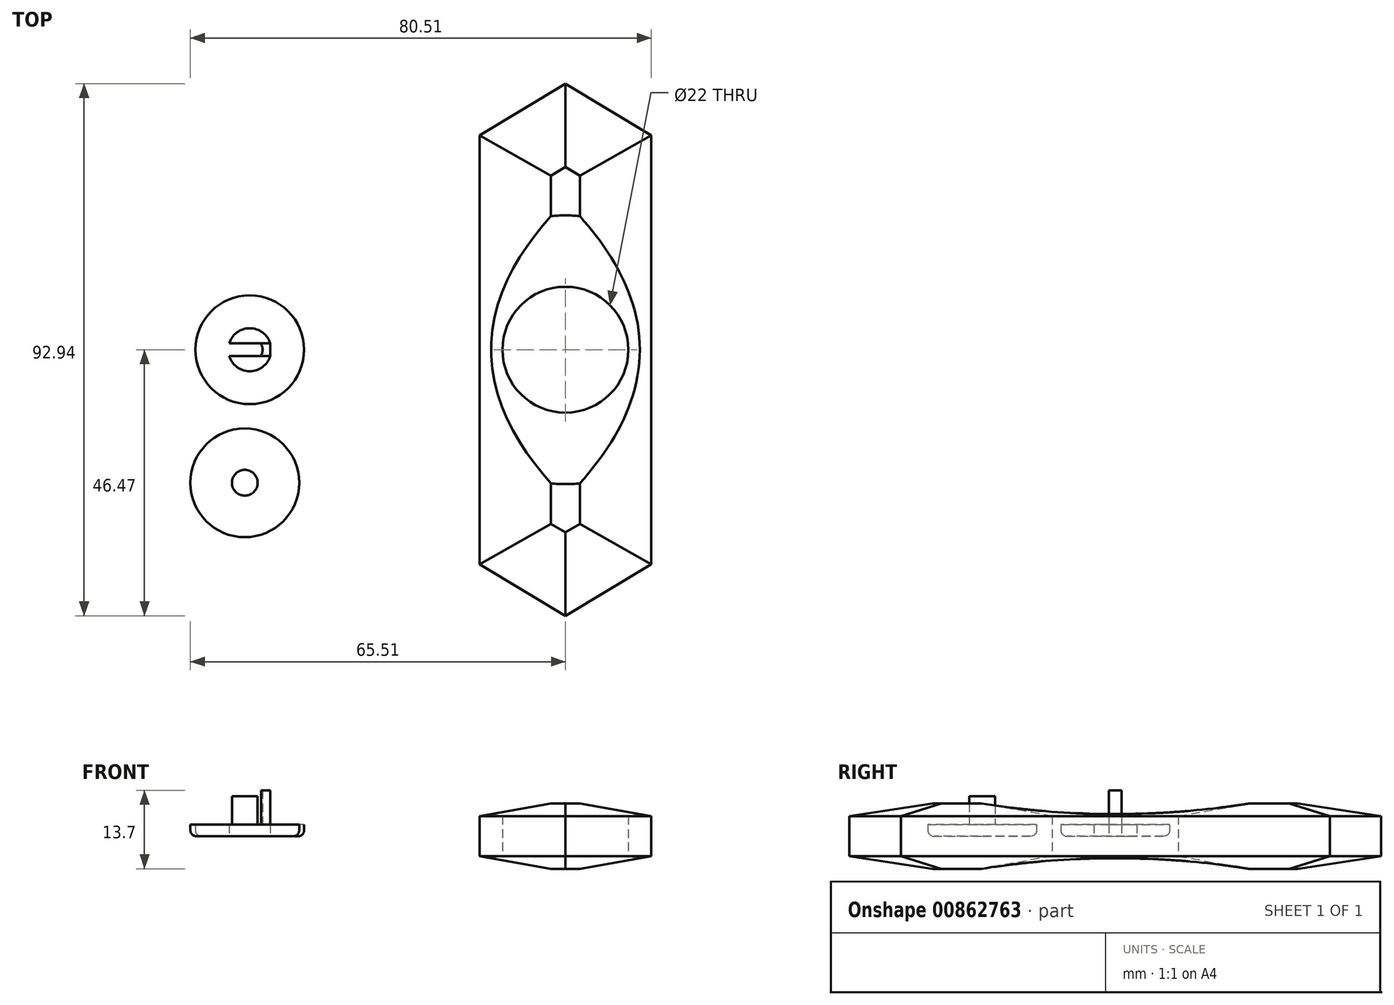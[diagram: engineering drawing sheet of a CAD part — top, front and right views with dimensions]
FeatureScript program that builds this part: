
annotation { "Feature Type Name" : "Feature", "Feature Type Description" : "" }
export const myFeature = defineFeature(function(context is Context, id is Id, definition is map)
    precondition{}
    {
        {
            var Q0;
            Q0=qCreatedBy(makeId("Top.planeOp"),FACE);
            var sketch = newSketch(context, id + "F0", { "sketchPlane" : qUnion([Q0])});
            skCircle(sketch, "E0", {"center": v(0, 0) * mm, "radius": 11 * mm});
            skLineSegment(sketch, "E1.left", {"start": v(15, -37.47) * mm, "end": v(15, 37.47) * mm});
            skLineSegment(sketch, "E1.right", {"start": v(-15, -37.47) * mm, "end": v(-15, 37.47) * mm});
            skLineSegment(sketch, "E2", {"start": v(-15, 37.47) * mm, "end": v(0, 46.47) * mm});
            skLineSegment(sketch, "E3", {"start": v(0, 46.47) * mm, "end": v(15, 37.47) * mm});
            skLineSegment(sketch, "E4", {"start": v(-15, -37.47) * mm, "end": v(0, -46.47) * mm});
            skLineSegment(sketch, "E5", {"start": v(0, -46.47) * mm, "end": v(15, -37.47) * mm});
            skSolve(sketch);
        }
        {
            var Q0;
            {var subQ0=sQuery(id+"F0.wireOp",EDGE,"E1.right");var subQ1=sQuery(id+"F0.wireOp",EDGE,"E1.top");var subQ2=makeQuery(id+"F0.imprint","INTERSECT",VERTEX,{"derivedFrom":[subQ1,subQ0]});Q0=makeQuery(id+"F0.imprint","IMPRINT",FACE,{"disambiguationData":[TD([[makeQuery(id+"F0.imprint","IMPRINT",EDGE,{"disambiguationData":[TD([[subQ2,1.0]])],"derivedFrom":subQ1}),1.0]])]});}
            var Q1;
            Q1=makeQuery(id+"F0.imprint","IMPRINT",FACE,{"disambiguationData":[TD([[makeQuery(id+"F0.imprint","IMPRINT",EDGE,{"derivedFrom":sQuery(id+"F0.wireOp",EDGE,"E0")}),-1.0]])]});
            var Q2;
            {var subQ0=sQuery(id+"F0.wireOp",EDGE,"XqkOnmEN-YKPt-X9L8-qTjw-NtbxfFgccqZy");var subQ1=sQuery(id+"F0.wireOp",EDGE,"E1.left");var subQ2=makeQuery(id+"F0.imprint","INTERSECT",VERTEX,{"disambiguationData":[OD(0.0)],"derivedFrom":[subQ1,subQ0]});Q2=makeQuery(id+"F0.imprint","IMPRINT",FACE,{"disambiguationData":[TD([[makeQuery(id+"F0.imprint","IMPRINT",EDGE,{"disambiguationData":[TD([[subQ2,-1.0]])],"derivedFrom":subQ1}),1.0]])]});}
            var Q3;
            {var subQ0=sQuery(id+"F0.wireOp",EDGE,"E1.left");var subQ1=sQuery(id+"F0.wireOp",EDGE,"E1.bottom");var subQ2=makeQuery(id+"F0.imprint","INTERSECT",VERTEX,{"derivedFrom":[subQ1,subQ0]});Q3=makeQuery(id+"F0.imprint","IMPRINT",FACE,{"disambiguationData":[TD([[makeQuery(id+"F0.imprint","IMPRINT",EDGE,{"disambiguationData":[TD([[subQ2,-1.0]])],"derivedFrom":subQ1}),-1.0]])]});}
            var Q4;
            {var subQ0=sQuery(id+"F0.wireOp",EDGE,"xUuo6eMj-NljG-XD0U-LhTG-hYgstR9SnbR7");var subQ1=sQuery(id+"F0.wireOp",EDGE,"E1.right");var subQ2=makeQuery(id+"F0.imprint","INTERSECT",VERTEX,{"disambiguationData":[OD(0.0)],"derivedFrom":[subQ1,subQ0]});Q4=makeQuery(id+"F0.imprint","IMPRINT",FACE,{"disambiguationData":[TD([[makeQuery(id+"F0.imprint","IMPRINT",EDGE,{"disambiguationData":[TD([[subQ2,-1.0]])],"derivedFrom":subQ1}),-1.0]])]});}
            var Q5;
            {var subQ0=sQuery(id+"F0.wireOp",EDGE,"XqkOnmEN-YKPt-X9L8-qTjw-NtbxfFgccqZy");var subQ1=sQuery(id+"F0.wireOp",EDGE,"E1.right");var subQ2=makeQuery(id+"F0.imprint","INTERSECT",VERTEX,{"disambiguationData":[OD(1.0)],"derivedFrom":[subQ1,subQ0]});Q5=makeQuery(id+"F0.imprint","IMPRINT",FACE,{"disambiguationData":[TD([[makeQuery(id+"F0.imprint","IMPRINT",EDGE,{"disambiguationData":[TD([[subQ2,-1.0]])],"derivedFrom":subQ1}),-1.0]])]});}
            var Q6;
            {var subQ0=sQuery(id+"F0.wireOp",EDGE,"XqkOnmEN-YKPt-X9L8-qTjw-NtbxfFgccqZy");var subQ1=sQuery(id+"F0.wireOp",EDGE,"E1.top");var subQ2=makeQuery(id+"F0.imprint","INTERSECT",VERTEX,{"derivedFrom":[subQ1,subQ0]});Q6=makeQuery(id+"F0.imprint","IMPRINT",FACE,{"disambiguationData":[TD([[makeQuery(id+"F0.imprint","IMPRINT",EDGE,{"disambiguationData":[TD([[subQ2,-1.0]])],"derivedFrom":subQ1}),1.0]])]});}
            var Q7;
            {var subQ0=sQuery(id+"F0.wireOp",EDGE,"E1.left");var subQ1=sQuery(id+"F0.wireOp",EDGE,"E1.top");var subQ2=makeQuery(id+"F0.imprint","INTERSECT",VERTEX,{"derivedFrom":[subQ1,subQ0]});Q7=makeQuery(id+"F0.imprint","IMPRINT",FACE,{"disambiguationData":[TD([[makeQuery(id+"F0.imprint","IMPRINT",EDGE,{"disambiguationData":[TD([[subQ2,-1.0]])],"derivedFrom":subQ1}),1.0]])]});}
            var Q8;
            {var subQ0=sQuery(id+"F0.wireOp",EDGE,"OLPtJjKp-UBlK-7H81-Stp1-wvhKm3npHkhX");var subQ1=sQuery(id+"F0.wireOp",EDGE,"E1.left");var subQ2=makeQuery(id+"F0.imprint","INTERSECT",VERTEX,{"disambiguationData":[OD(0.0)],"derivedFrom":[subQ1,subQ0]});Q8=makeQuery(id+"F0.imprint","IMPRINT",FACE,{"disambiguationData":[TD([[makeQuery(id+"F0.imprint","IMPRINT",EDGE,{"disambiguationData":[TD([[subQ2,-1.0]])],"derivedFrom":subQ1}),1.0]])]});}
            var Q9;
            {var subQ0=sQuery(id+"F0.wireOp",EDGE,"E1.right");var subQ1=sQuery(id+"F0.wireOp",EDGE,"E1.bottom");var subQ2=makeQuery(id+"F0.imprint","INTERSECT",VERTEX,{"derivedFrom":[subQ1,subQ0]});Q9=makeQuery(id+"F0.imprint","IMPRINT",FACE,{"disambiguationData":[TD([[makeQuery(id+"F0.imprint","IMPRINT",EDGE,{"disambiguationData":[TD([[subQ2,1.0]])],"derivedFrom":subQ1}),-1.0]])]});}
            var Q10;
            {var subQ0=sQuery(id+"F0.wireOp",EDGE,"XqkOnmEN-YKPt-X9L8-qTjw-NtbxfFgccqZy");var subQ1=sQuery(id+"F0.wireOp",EDGE,"E1.bottom");var subQ2=makeQuery(id+"F0.imprint","INTERSECT",VERTEX,{"derivedFrom":[subQ1,subQ0]});Q10=makeQuery(id+"F0.imprint","IMPRINT",FACE,{"disambiguationData":[TD([[makeQuery(id+"F0.imprint","IMPRINT",EDGE,{"disambiguationData":[TD([[subQ2,-1.0]])],"derivedFrom":subQ1}),-1.0]])]});}
            var Q11;
            {var subQ0=sQuery(id+"F0.wireOp",EDGE,"tDE5TlyR-l5bq-vjll-LGqx-ABghjxnvdLlJ");var subQ1=sQuery(id+"F0.wireOp",EDGE,"E1.left");var subQ2=makeQuery(id+"F0.imprint","INTERSECT",VERTEX,{"disambiguationData":[OD(0.0)],"derivedFrom":[subQ1,subQ0]});Q11=makeQuery(id+"F0.imprint","IMPRINT",FACE,{"disambiguationData":[TD([[makeQuery(id+"F0.imprint","IMPRINT",EDGE,{"disambiguationData":[TD([[subQ2,-1.0]])],"derivedFrom":subQ1}),1.0]])]});}
            var Q12;
            {var subQ1=sQuery(id+"F0.wireOp",EDGE,"XqkOnmEN-YKPt-X9L8-qTjw-NtbxfFgccqZy");var subQ3=sQuery(id+"F0.wireOp",EDGE,"E1.bottom");var subQ4=makeQuery(id+"F0.imprint","INTERSECT",VERTEX,{"derivedFrom":[subQ3,subQ1]});Q12=makeQuery(id+"F0.imprint","IMPRINT",FACE,{"disambiguationData":[TD([[makeQuery(id+"F0.imprint","IMPRINT",EDGE,{"disambiguationData":[TD([[subQ4,-1.0]])],"derivedFrom":subQ3}),1.0]])]});}
            var Q13;
            {var subQ5=sQuery(id+"F0.wireOp",EDGE,"XqkOnmEN-YKPt-X9L8-qTjw-NtbxfFgccqZy");var subQ7=sQuery(id+"F0.wireOp",EDGE,"E1.top");var subQ8=makeQuery(id+"F0.imprint","INTERSECT",VERTEX,{"derivedFrom":[subQ7,subQ5]});Q13=makeQuery(id+"F0.imprint","IMPRINT",FACE,{"disambiguationData":[TD([[makeQuery(id+"F0.imprint","IMPRINT",EDGE,{"disambiguationData":[TD([[subQ8,-1.0]])],"derivedFrom":subQ7}),-1.0]])]});}
            extrude(context, id + "F1", {"entities" : qUnion([Q0, Q1, Q2, Q3, Q4, Q5, Q6, Q7, Q8, Q9, Q10, Q11, Q12, Q13]), "endBound" : BoundingType.SYMMETRIC, "depth" : 7 * mm, "offsetDistance" : 25 * mm});
        }
        {
            var Q0;
            Q0=qCreatedBy(makeId("Top.planeOp"),FACE);
            var sketch = newSketch(context, id + "F2", { "sketchPlane" : qUnion([Q0])});
            skCircle(sketch, "E6", {"center": v(-55.14, 0) * mm, "radius": 3.75 * mm});
            skCircle(sketch, "E7", {"center": v(-55.14, 0) * mm, "radius": 2.25 * mm});
            skCircle(sketch, "E8", {"center": v(-55.14, 0) * mm, "radius": 9.5 * mm});
            skLineSegment(sketch, "E9.bottom", {"start": v(-51.56, -1.1) * mm, "end": v(-58.73, -1.1) * mm});
            skLineSegment(sketch, "E9.top", {"start": v(-51.56, 1.1) * mm, "end": v(-58.73, 1.1) * mm});
            skLineSegment(sketch, "E9.left", {"start": v(-51.56, -1.1) * mm, "end": v(-51.56, 1.1) * mm});
            skLineSegment(sketch, "E9.right", {"start": v(-58.73, -1.1) * mm, "end": v(-58.73, 1.1) * mm});
            skSolve(sketch);
        }
        {
            var Q0;
            {var subQ0=sQuery(id+"F2.wireOp",EDGE,"E9.bottom");var subQ4=sQuery(id+"F2.wireOp",EDGE,"E7");var subQ5=makeQuery(id+"F2.imprint","INTERSECT",VERTEX,{"disambiguationData":[OD(0.0)],"derivedFrom":[subQ4,subQ0]});Q0=makeQuery(id+"F2.imprint","IMPRINT",FACE,{"disambiguationData":[TD([[makeQuery(id+"F2.imprint","IMPRINT",EDGE,{"disambiguationData":[TD([[subQ5,-1.0]])],"derivedFrom":subQ4}),-1.0]])]});}
            var Q1;
            {var subQ0=sQuery(id+"F2.wireOp",EDGE,"E9.top");var subQ4=sQuery(id+"F2.wireOp",EDGE,"E7");var subQ5=makeQuery(id+"F2.imprint","INTERSECT",VERTEX,{"disambiguationData":[OD(0.0)],"derivedFrom":[subQ4,subQ0]});Q1=makeQuery(id+"F2.imprint","IMPRINT",FACE,{"disambiguationData":[TD([[makeQuery(id+"F2.imprint","IMPRINT",EDGE,{"disambiguationData":[TD([[subQ5,1.0]])],"derivedFrom":subQ4}),-1.0]])]});}
            extrude(context, id + "F3", {"entities" : qUnion([Q0, Q1]), "depth" : 8 * mm, "offsetDistance" : 25 * mm});
        }
        {
            var Q0;
            Q0 = qSketchRegion(id + "F2", true);
            var Q1;
            Q1=makeQuery(id+"F2.imprint","IMPRINT",FACE,{"disambiguationData":[TD([[makeQuery(id+"F2.imprint","IMPRINT",EDGE,{"derivedFrom":sQuery(id+"F2.wireOp",EDGE,"E7")}),1.0]])]});
            var Q2;
            {var subQ5=sQuery(id+"F2.wireOp",EDGE,"E9.left");Q2=makeQuery(id+"F2.imprint","IMPRINT",FACE,{"disambiguationData":[TD([[makeQuery(id+"F2.imprint","IMPRINT",EDGE,{"derivedFrom":subQ5}),1.0]])]});}
            var Q3;
            {var subQ0=sQuery(id+"F2.wireOp",EDGE,"E9.top");var subQ1=sQuery(id+"F2.wireOp",EDGE,"E7");var subQ2=makeQuery(id+"F2.imprint","INTERSECT",VERTEX,{"disambiguationData":[OD(0.0)],"derivedFrom":[subQ1,subQ0]});Q3=makeQuery(id+"F2.imprint","IMPRINT",FACE,{"disambiguationData":[TD([[makeQuery(id+"F2.imprint","IMPRINT",EDGE,{"disambiguationData":[TD([[subQ2,1.0]])],"derivedFrom":subQ1}),1.0]])]});}
            var Q4;
            {var subQ0=sQuery(id+"F2.wireOp",EDGE,"E9.bottom");var subQ1=sQuery(id+"F2.wireOp",EDGE,"E7");var subQ2=makeQuery(id+"F2.imprint","INTERSECT",VERTEX,{"disambiguationData":[OD(0.0)],"derivedFrom":[subQ1,subQ0]});Q4=makeQuery(id+"F2.imprint","IMPRINT",FACE,{"disambiguationData":[TD([[makeQuery(id+"F2.imprint","IMPRINT",EDGE,{"disambiguationData":[TD([[subQ2,-1.0]])],"derivedFrom":subQ1}),1.0]])]});}
            var Q5;
            {var subQ0=sQuery(id+"F2.wireOp",EDGE,"E9.right");Q5=makeQuery(id+"F2.imprint","IMPRINT",FACE,{"disambiguationData":[TD([[makeQuery(id+"F2.imprint","IMPRINT",EDGE,{"derivedFrom":subQ0}),1.0]])]});}
            var Q6;
            {var subQ5=sQuery(id+"F2.wireOp",EDGE,"E9.right");Q6=makeQuery(id+"F2.imprint","IMPRINT",FACE,{"disambiguationData":[TD([[makeQuery(id+"F2.imprint","IMPRINT",EDGE,{"derivedFrom":subQ5}),-1.0]])]});}
            var Q7;
            {var subQ0=sQuery(id+"F2.wireOp",EDGE,"E9.left");Q7=makeQuery(id+"F2.imprint","IMPRINT",FACE,{"disambiguationData":[TD([[makeQuery(id+"F2.imprint","IMPRINT",EDGE,{"derivedFrom":subQ0}),-1.0]])]});}
            extrude(context, id + "F4", {"entities" : qUnion([Q0, Q1, Q2, Q3, Q4, Q5, Q6, Q7]), "operationType" : NewBodyOperationType.ADD, "depth" : 2 * mm, "offsetDistance" : 25 * mm});
        }
        {
            var Q0;
            Q0=makeQuery(id+"F4.opExtrude","CAP_EDGE",EDGE,{"disambiguationData":[OSD([sQuery(id+"F2.wireOp",EDGE,"E8")])],"isStart":true});
            fillet(context, id + "F5", {"entities" : qUnion([Q0]), "radius" : 1 * mm, "tangentPropagation" : true, "allowEdgeOverflow" : false});
        }
        {
            var Q0;
            Q0=qCreatedBy(makeId("Top.planeOp"),FACE);
            var sketch = newSketch(context, id + "F6", { "sketchPlane" : qUnion([Q0])});
            skCircle(sketch, "E10", {"center": v(-56, -23.24) * mm, "radius": 2.25 * mm});
            skCircle(sketch, "E11", {"center": v(-56, -23.24) * mm, "radius": 9.5 * mm});
            skSolve(sketch);
        }
        {
            var Q0;
            Q0=makeQuery(id+"F6.imprint","IMPRINT",FACE,{"disambiguationData":[TD([[makeQuery(id+"F6.imprint","IMPRINT",EDGE,{"derivedFrom":sQuery(id+"F6.wireOp",EDGE,"E10")}),-1.0]])]});
            extrude(context, id + "F7", {"entities" : qUnion([Q0]), "depth" : 2 * mm, "offsetDistance" : 25 * mm});
        }
        {
            var Q0;
            Q0=makeQuery(id+"F6.imprint","IMPRINT",FACE,{"disambiguationData":[TD([[makeQuery(id+"F6.imprint","IMPRINT",EDGE,{"derivedFrom":sQuery(id+"F6.wireOp",EDGE,"E10")}),1.0]])]});
            extrude(context, id + "F8", {"entities" : qUnion([Q0]), "operationType" : NewBodyOperationType.ADD, "depth" : 7 * mm, "offsetDistance" : 25 * mm});
        }
        {
            var Q0;
            Q0=makeQuery(id+"F7.opExtrude","CAP_EDGE",EDGE,{"disambiguationData":[OSD([sQuery(id+"F6.wireOp",EDGE,"E11")])],"isStart":true});
            fillet(context, id + "F9", {"entities" : qUnion([Q0]), "radius" : 1 * mm, "tangentPropagation" : true, "allowEdgeOverflow" : false});
        }
        {
            var Q0;
            Q0=makeQuery(id+"F1.opExtrude","CAP_FACE",FACE,{"disambiguationData":[OSD([sQuery(id+"F0.wireOp",EDGE,"E0"),sQuery(id+"F0.wireOp",EDGE,"E1.left"),sQuery(id+"F0.wireOp",EDGE,"E1.right"),sQuery(id+"F0.wireOp",EDGE,"E2"),sQuery(id+"F0.wireOp",EDGE,"E3"),sQuery(id+"F0.wireOp",EDGE,"E4"),sQuery(id+"F0.wireOp",EDGE,"E5")])],"isStart":false});
            var Q1;
            Q1=makeQuery(id+"F1.opExtrude","CAP_FACE",FACE,{"disambiguationData":[OSD([sQuery(id+"F0.wireOp",EDGE,"E0"),sQuery(id+"F0.wireOp",EDGE,"E1.left"),sQuery(id+"F0.wireOp",EDGE,"E1.right"),sQuery(id+"F0.wireOp",EDGE,"E2"),sQuery(id+"F0.wireOp",EDGE,"E3"),sQuery(id+"F0.wireOp",EDGE,"E4"),sQuery(id+"F0.wireOp",EDGE,"E5")])],"isStart":true});
            extrude(context, id + "F10", {"entities" : qUnion([Q0, Q1]), "operationType" : NewBodyOperationType.ADD, "endBound" : BoundingType.SYMMETRIC, "depth" : 4.4 * mm, "offsetDistance" : 25 * mm, "hasDraft" : true, "draftAngle" : 80 * degree, "draftPullDirection" : true});
        }
    });
